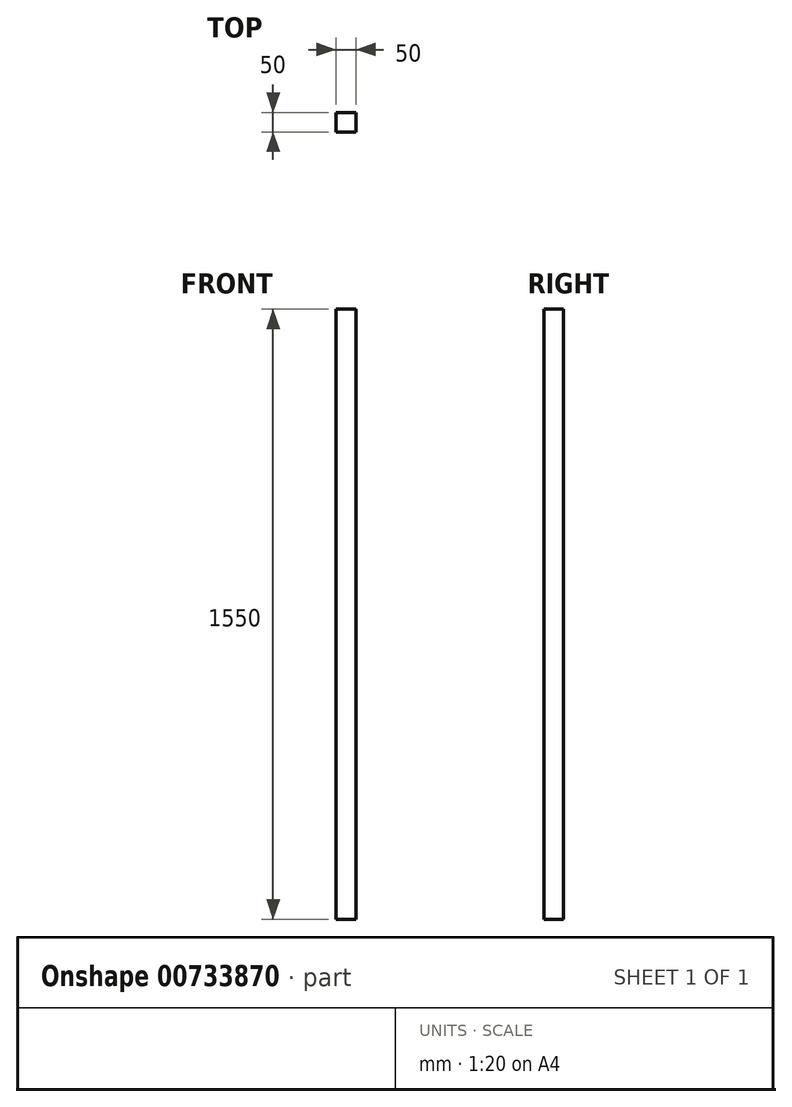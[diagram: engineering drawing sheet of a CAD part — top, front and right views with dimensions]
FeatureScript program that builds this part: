
annotation { "Feature Type Name" : "Feature", "Feature Type Description" : "" }
export const myFeature = defineFeature(function(context is Context, id is Id, definition is map)
    precondition{}
    {
        {
            var Q0;
            Q0=qCreatedBy(makeId("Top.planeOp"),FACE);
            var sketch = newSketch(context, id + "F0", { "sketchPlane" : qUnion([Q0])});
            skLineSegment(sketch, "E0.bottom", {"start": v(25, 25) * mm, "end": v(-25, 25) * mm});
            skLineSegment(sketch, "E0.top", {"start": v(25, -25) * mm, "end": v(-25, -25) * mm});
            skLineSegment(sketch, "E0.left", {"start": v(25, 25) * mm, "end": v(25, -25) * mm});
            skLineSegment(sketch, "E0.right", {"start": v(-25, 25) * mm, "end": v(-25, -25) * mm});
            skPoint(sketch, "E0.middle", {"position": v(0, 0) * mm});
            skLineSegment(sketch, "E1.bottom", {"start": v(24, 24) * mm, "end": v(-24, 24) * mm});
            skLineSegment(sketch, "E1.top", {"start": v(24, -24) * mm, "end": v(-24, -24) * mm});
            skLineSegment(sketch, "E1.left", {"start": v(24, 24) * mm, "end": v(24, -24) * mm});
            skLineSegment(sketch, "E1.right", {"start": v(-24, 24) * mm, "end": v(-24, -24) * mm});
            skSolve(sketch);
        }
        {
            var Q0;
            Q0=makeQuery(id+"F0.imprint","IMPRINT",FACE,{"disambiguationData":[TD([[makeQuery(id+"F0.imprint","IMPRINT",EDGE,{"derivedFrom":sQuery(id+"F0.wireOp",EDGE,"E0.bottom")}),1.0]])]});
            extrude(context, id + "F1", {"entities" : qUnion([Q0]), "depth" : 1550 * mm, "offsetDistance" : 25 * mm});
        }
        {
            var Q0;
            Q0=makeQuery(id+"F1.opExtrude","CAP_FACE",FACE,{"disambiguationData":[OSD([sQuery(id+"F0.wireOp",EDGE,"E0.bottom"),sQuery(id+"F0.wireOp",EDGE,"E0.top"),sQuery(id+"F0.wireOp",EDGE,"E0.left"),sQuery(id+"F0.wireOp",EDGE,"E0.right"),sQuery(id+"F0.wireOp",EDGE,"E1.bottom"),sQuery(id+"F0.wireOp",EDGE,"E1.top"),sQuery(id+"F0.wireOp",EDGE,"E1.left"),sQuery(id+"F0.wireOp",EDGE,"E1.right")])],"isStart":false});
            var sketch = newSketch(context, id + "F2", { "sketchPlane" : qUnion([Q0])});
            skLineSegment(sketch, "E2.bottom", {"start": v(-24, -24) * mm, "end": v(24, -24) * mm});
            skLineSegment(sketch, "E2.top", {"start": v(-24, 24) * mm, "end": v(24, 24) * mm});
            skLineSegment(sketch, "E2.left", {"start": v(-24, -24) * mm, "end": v(-24, 24) * mm});
            skLineSegment(sketch, "E2.right", {"start": v(24, -24) * mm, "end": v(24, 24) * mm});
            skSolve(sketch);
        }
        {
            var Q0;
            Q0=makeQuery(id+"F2.imprint","IMPRINT",FACE,{"disambiguationData":[TD([[makeQuery(id+"F2.imprint","IMPRINT",EDGE,{"derivedFrom":sQuery(id+"F2.wireOp",EDGE,"E2.bottom")}),-1.0]])]});
            extrude(context, id + "F3", {"entities" : qUnion([Q0]), "operationType" : NewBodyOperationType.ADD, "oppositeDirection" : true, "depth" : 1 * mm, "offsetDistance" : 25 * mm});
        }
    });
